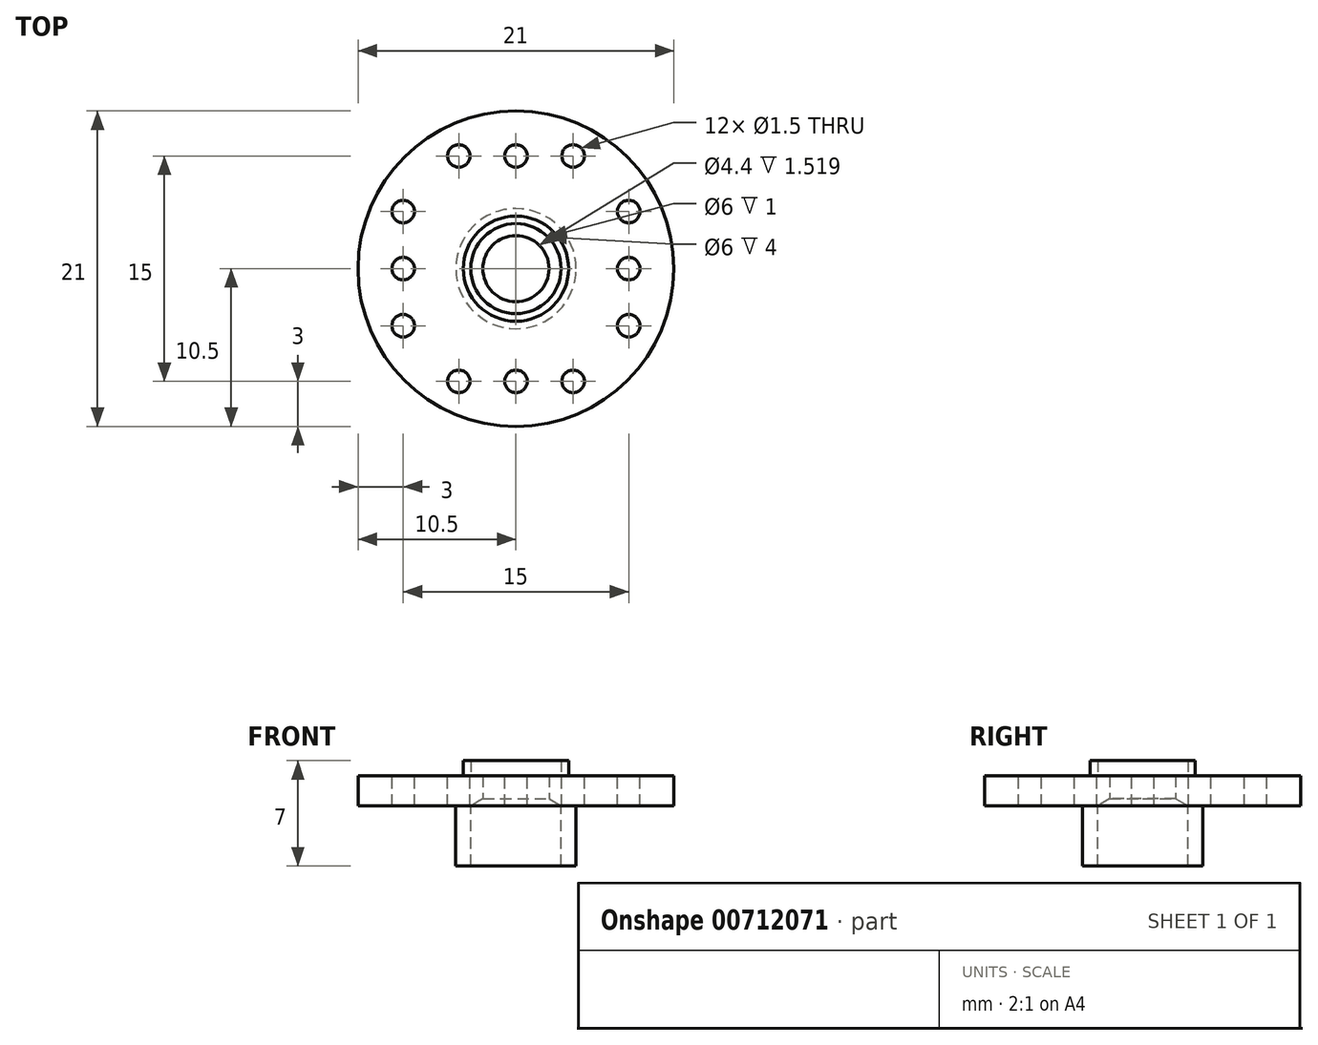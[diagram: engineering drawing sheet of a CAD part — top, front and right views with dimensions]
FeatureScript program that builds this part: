
annotation { "Feature Type Name" : "Feature", "Feature Type Description" : "" }
export const myFeature = defineFeature(function(context is Context, id is Id, definition is map)
    precondition{}
    {
        {
            var Q0;
            Q0=qCreatedBy(makeId("Top.planeOp"),FACE);
            var sketch = newSketch(context, id + "F0", { "sketchPlane" : qUnion([Q0])});
            skCircle(sketch, "E0", {"center": v(0, 0) * mm, "radius": 10.5 * mm});
            skCircle(sketch, "E1", {"center": v(0, 0) * mm, "radius": 7.5 * mm, "construction": true});
            skLineSegment(sketch, "E2", {"start": v(0, 7.5) * mm, "end": v(3.8, 7.5) * mm, "construction": true});
            skCircle(sketch, "E3", {"center": v(3.8, 7.5) * mm, "radius": 0.75 * mm});
            skCircle(sketch, "E4", {"center": v(0, 7.5) * mm, "radius": 0.75 * mm});
            skCircle(sketch, "E5.MirrorC", {"center": v(-3.8, 7.5) * mm, "radius": 0.75 * mm});
            skLineSegment(sketch, "E6", {"start": v(0, 7.5) * mm, "end": v(-3.8, 7.5) * mm, "construction": true});
            skCircle(sketch, "E7.1.0", {"center": v(7.5, 3.8) * mm, "radius": 0.75 * mm});
            skCircle(sketch, "E7.1.1", {"center": v(7.5, 0) * mm, "radius": 0.75 * mm});
            skCircle(sketch, "E7.1.2", {"center": v(7.5, -3.8) * mm, "radius": 0.75 * mm});
            skCircle(sketch, "E7.2.0", {"center": v(3.8, -7.5) * mm, "radius": 0.75 * mm});
            skCircle(sketch, "E7.2.1", {"center": v(0, -7.5) * mm, "radius": 0.75 * mm});
            skCircle(sketch, "E7.2.2", {"center": v(-3.8, -7.5) * mm, "radius": 0.75 * mm});
            skCircle(sketch, "E7.3.0", {"center": v(-7.5, -3.8) * mm, "radius": 0.75 * mm});
            skCircle(sketch, "E7.3.1", {"center": v(-7.5, 0) * mm, "radius": 0.75 * mm});
            skCircle(sketch, "E7.3.2", {"center": v(-7.5, 3.8) * mm, "radius": 0.75 * mm});
            skLineSegment(sketch, "E7.anchor1", {"start": v(0, 0) * mm, "end": v(-3.8, 7.5) * mm, "construction": true});
            skLineSegment(sketch, "E7.anchor2", {"start": v(0, 0) * mm, "end": v(-7.5, -3.8) * mm, "construction": true});
            skCircle(sketch, "E8", {"center": v(0, 0) * mm, "radius": 3.5 * mm});
            skCircle(sketch, "E9.0", {"center": v(0, 0) * mm, "radius": 3 * mm});
            skSolve(sketch);
        }
        {
            var Q0;
            Q0 = qSketchRegion(id + "F0", true);
            var Q1;
            Q1=makeQuery(id+"F0.imprint","IMPRINT",FACE,{"disambiguationData":[TD([[makeQuery(id+"F0.imprint","IMPRINT",EDGE,{"derivedFrom":sQuery(id+"F0.wireOp",EDGE,"E9.0")}),1.0]])]});
            var Q2;
            Q2=makeQuery(id+"F0.imprint","IMPRINT",FACE,{"disambiguationData":[TD([[makeQuery(id+"F0.imprint","IMPRINT",EDGE,{"derivedFrom":sQuery(id+"F0.wireOp",EDGE,"E8")}),1.0]])]});
            extrude(context, id + "F1", {"entities" : qUnion([Q0, Q1, Q2]), "oppositeDirection" : true, "depth" : 2 * mm, "offsetDistance" : 25 * mm});
        }
        {
            var Q0;
            Q0=makeQuery(id+"F0.imprint","IMPRINT",FACE,{"disambiguationData":[TD([[makeQuery(id+"F0.imprint","IMPRINT",EDGE,{"derivedFrom":sQuery(id+"F0.wireOp",EDGE,"E8")}),1.0]])]});
            extrude(context, id + "F2", {"entities" : qUnion([Q0]), "operationType" : NewBodyOperationType.ADD, "depth" : 1 * mm, "offsetDistance" : 25 * mm});
        }
        {
            var Q0;
            Q0=makeQuery(id+"F1.opExtrude","CAP_FACE",FACE,{"disambiguationData":[OSD([sQuery(id+"F0.wireOp",EDGE,"E0"),sQuery(id+"F0.wireOp",EDGE,"E3"),sQuery(id+"F0.wireOp",EDGE,"E4"),sQuery(id+"F0.wireOp",EDGE,"E5.MirrorC"),sQuery(id+"F0.wireOp",EDGE,"E7.1.0"),sQuery(id+"F0.wireOp",EDGE,"E7.1.1"),sQuery(id+"F0.wireOp",EDGE,"E7.1.2"),sQuery(id+"F0.wireOp",EDGE,"E7.2.0"),sQuery(id+"F0.wireOp",EDGE,"E7.2.1"),sQuery(id+"F0.wireOp",EDGE,"E7.2.2"),sQuery(id+"F0.wireOp",EDGE,"E7.3.0"),sQuery(id+"F0.wireOp",EDGE,"E7.3.1"),sQuery(id+"F0.wireOp",EDGE,"E7.3.2")])],"isStart":false});
            var sketch = newSketch(context, id + "F3", { "sketchPlane" : qUnion([Q0])});
            skCircle(sketch, "E10", {"center": v(0, 0) * mm, "radius": 4 * mm});
            skSolve(sketch);
        }
        {
            var Q0;
            Q0=makeQuery(id+"F3.imprint","IMPRINT",FACE,{"disambiguationData":[TD([[makeQuery(id+"F3.imprint","IMPRINT",EDGE,{"derivedFrom":sQuery(id+"F3.wireOp",EDGE,"E10")}),1.0]])]});
            extrude(context, id + "F4", {"entities" : qUnion([Q0]), "operationType" : NewBodyOperationType.ADD, "depth" : 4 * mm, "offsetDistance" : 25 * mm});
        }
        {
            var Q0;
            Q0=qCreatedBy(makeId("Front.planeOp"),FACE);
            var sketch = newSketch(context, id + "F5", { "sketchPlane" : qUnion([Q0])});
            skLineSegment(sketch, "E11", {"start": v(0, 0) * mm, "end": v(-3.5, 0) * mm, "construction": true});
            skLineSegment(sketch, "E12", {"start": v(-3.5, 0) * mm, "end": v(-4.5, 0) * mm});
            skLineSegment(sketch, "E13", {"start": v(-3.5, 1) * mm, "end": v(-4.5, 0) * mm});
            skLineSegment(sketch, "E14", {"start": v(-3.5, 1) * mm, "end": v(-3.5, 0) * mm});
            skSolve(sketch);
        }
        {
            var Q0;
            Q0=sQuery(id+"F0.wireOp",VERTEX,"E0.center");
            var Q1;
            Q1=makeQuery(id+"F1.opExtrude","SWEPT_BODY",BODY,{"disambiguationData":[OSD([sQuery(id+"F0.wireOp",EDGE,"E0"),sQuery(id+"F0.wireOp",EDGE,"E3"),sQuery(id+"F0.wireOp",EDGE,"E4"),sQuery(id+"F0.wireOp",EDGE,"E5.MirrorC"),sQuery(id+"F0.wireOp",EDGE,"E7.1.0"),sQuery(id+"F0.wireOp",EDGE,"E7.1.1"),sQuery(id+"F0.wireOp",EDGE,"E7.1.2"),sQuery(id+"F0.wireOp",EDGE,"E7.2.0"),sQuery(id+"F0.wireOp",EDGE,"E7.2.1"),sQuery(id+"F0.wireOp",EDGE,"E7.2.2"),sQuery(id+"F0.wireOp",EDGE,"E7.3.0"),sQuery(id+"F0.wireOp",EDGE,"E7.3.1"),sQuery(id+"F0.wireOp",EDGE,"E7.3.2")])]});
            hole(context, id + "F6", {"style" : HoleStyle.SIMPLE, "endStyle" : HoleEndStyle.THROUGH, "standardTappedOrClearance" : lookupTablePath({ "standard" : "ISO", "fit" : "Normal", "size" : "M4", "type" : "Clearance" }), "standardBlindInLast" : lookupTablePath({ "fit" : "Standard", "standard" : "ISO", "size" : "M4", "type" : "Clearance" }), "holeDiameter" : 4.4 * mm, "majorDiameter" : 5 * mm, "isTappedThrough" : true, "tappedDepth" : 12 * mm, "tapClearance" : 3, "locations" : qUnion([Q0]), "scope" : qUnion([Q1]), "startStyle" : HoleStartStyle.PART});
        }
        {
            var Q0;
            Q0=makeQuery(id+"F4.opExtrude","CAP_FACE",FACE,{"disambiguationData":[OSD([sQuery(id+"F3.wireOp",EDGE,"E10")])],"isStart":false});
            var sketch = newSketch(context, id + "F7", { "sketchPlane" : qUnion([Q0])});
            skLineSegment(sketch, "E15", {"start": v(0, 0) * mm, "end": v(-4, 0) * mm, "construction": true});
            skSolve(sketch);
        }
        {
            var Q0;
            Q0=sQuery(id+"F7.wireOp",VERTEX,"E15.start");
            var Q1;
            Q1=makeQuery(id+"F1.opExtrude","SWEPT_BODY",BODY,{"disambiguationData":[OSD([sQuery(id+"F0.wireOp",EDGE,"E0"),sQuery(id+"F0.wireOp",EDGE,"E3"),sQuery(id+"F0.wireOp",EDGE,"E4"),sQuery(id+"F0.wireOp",EDGE,"E5.MirrorC"),sQuery(id+"F0.wireOp",EDGE,"E7.1.0"),sQuery(id+"F0.wireOp",EDGE,"E7.1.1"),sQuery(id+"F0.wireOp",EDGE,"E7.1.2"),sQuery(id+"F0.wireOp",EDGE,"E7.2.0"),sQuery(id+"F0.wireOp",EDGE,"E7.2.1"),sQuery(id+"F0.wireOp",EDGE,"E7.2.2"),sQuery(id+"F0.wireOp",EDGE,"E7.3.0"),sQuery(id+"F0.wireOp",EDGE,"E7.3.1"),sQuery(id+"F0.wireOp",EDGE,"E7.3.2")])]});
            hole(context, id + "F8", {"style" : HoleStyle.SIMPLE, "endStyle" : HoleEndStyle.BLIND, "holeDiameter" : 6 * mm, "majorDiameter" : 5 * mm, "holeDepth" : 4 * mm, "isTappedThrough" : true, "tappedDepth" : 12 * mm, "tapClearance" : 3, "locations" : qUnion([Q0]), "scope" : qUnion([Q1]), "startStyle" : HoleStartStyle.PART});
        }
    });
